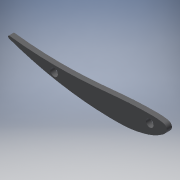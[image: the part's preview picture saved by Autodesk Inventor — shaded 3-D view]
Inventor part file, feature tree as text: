
AUTODESK INVENTOR PART (.ipt)
format: ipt  version: 2018.2 (Build 222227000, 227)  size: 137,728 bytes
history: native  units: mm
features: extrude x2, sketch x2, other x1, projected_geometry x1
ambient origin geometry x8: Origin, YZ Plane, XZ Plane, XY Plane, X Axis, Y Axis, Z Axis, Center Point
bodies: Body1 (feature_tree)
feature tree (6):
  extrude  "押し出し1"  Depth=4.0mm TaperAngle=0.0deg
  extrude  "押し出し2"  Depth=6.0mm
  other  "厚み1"
  sketch  "スケッチ1"
  projected_geometry  "投影ループ1"
  sketch  "スケッチ2"
